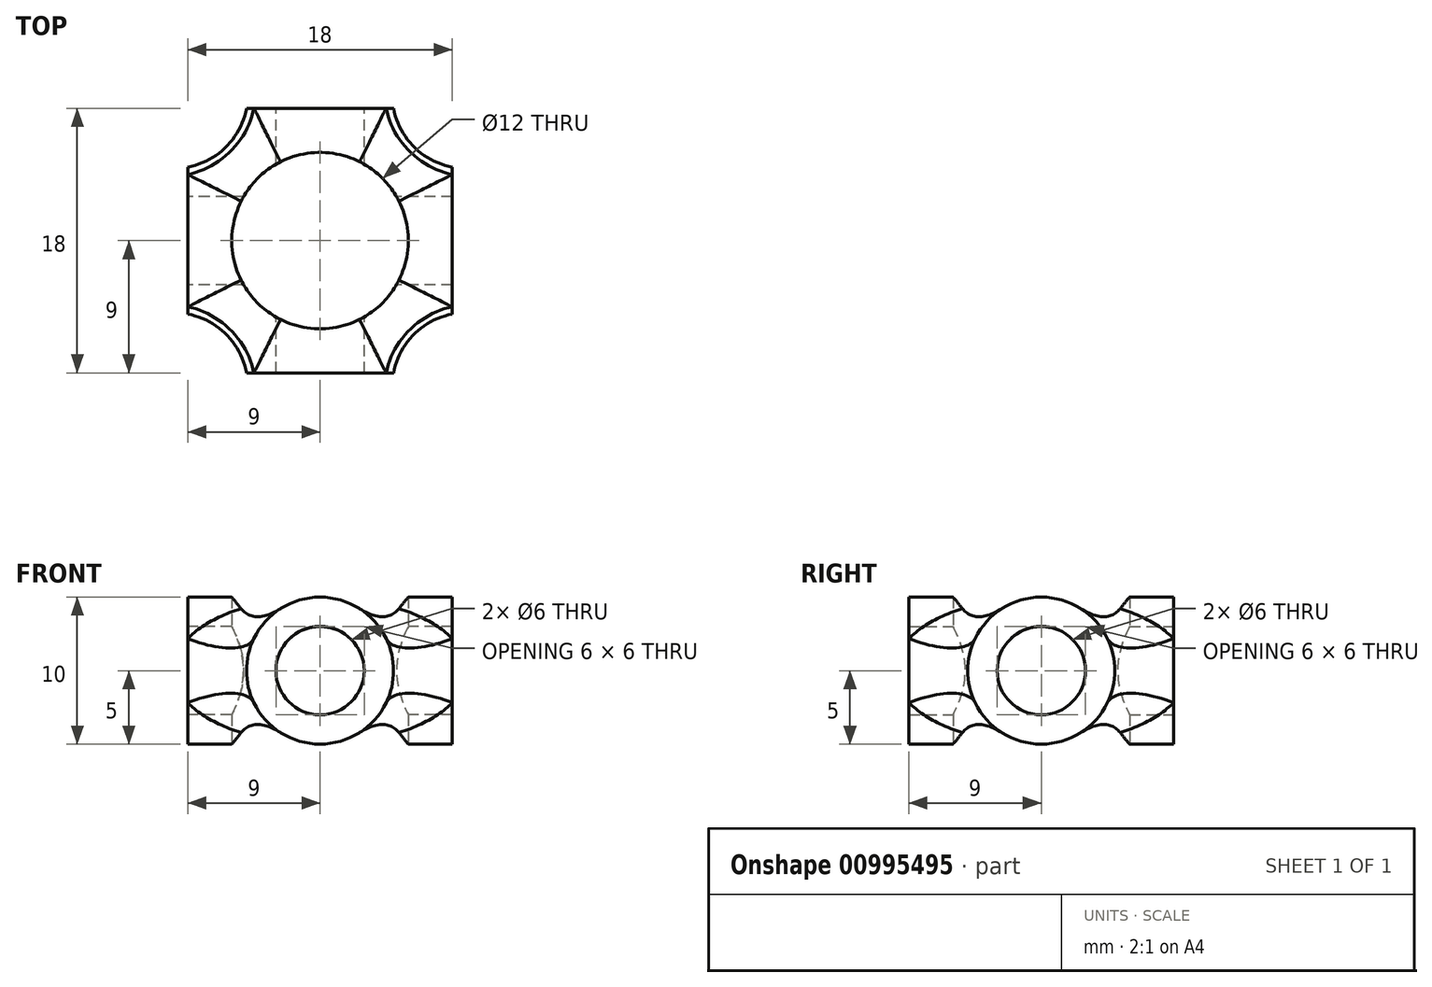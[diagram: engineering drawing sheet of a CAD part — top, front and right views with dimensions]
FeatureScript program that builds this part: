
annotation { "Feature Type Name" : "Feature", "Feature Type Description" : "" }
export const myFeature = defineFeature(function(context is Context, id is Id, definition is map)
    precondition{}
    {
        {
            var Q0;
            Q0=qCreatedBy(makeId("Front.planeOp"),FACE);
            var sketch = newSketch(context, id + "F0", { "sketchPlane" : qUnion([Q0])});
            skCircle(sketch, "E0", {"center": v(0, 0) * mm, "radius": 3 * mm});
            skCircle(sketch, "E1", {"center": v(0, 0) * mm, "radius": 5 * mm});
            skSolve(sketch);
        }
        {
            var Q0;
            Q0 = qSketchRegion(id + "F0", true);
            extrude(context, id + "F1", {"entities" : qUnion([Q0]), "endBound" : BoundingType.SYMMETRIC, "depth" : 18 * mm, "offsetDistance" : 25 * mm});
        }
        {
            var Q0;
            Q0=qCreatedBy(makeId("Right.planeOp"),FACE);
            var sketch = newSketch(context, id + "F2", { "sketchPlane" : qUnion([Q0])});
            skCircle(sketch, "E2", {"center": v(0, 0) * mm, "radius": 5 * mm});
            skCircle(sketch, "E3", {"center": v(0, 0) * mm, "radius": 3 * mm});
            skSolve(sketch);
        }
        {
            var Q0;
            Q0 = qSketchRegion(id + "F2", true);
            extrude(context, id + "F3", {"entities" : qUnion([Q0]), "operationType" : NewBodyOperationType.ADD, "endBound" : BoundingType.SYMMETRIC, "depth" : 18 * mm, "offsetDistance" : 25 * mm});
        }
        {
            var Q0;
            Q0=makeQuery(id+"F3.boolean.opBoolean","INTERSECT",EDGE,{"disambiguationData":[OD(2.0)],"derivedFrom":[makeQuery(id+"F1.opExtrude","SWEPT_FACE",FACE,{"disambiguationData":[OSD([sQuery(id+"F0.wireOp",EDGE,"E1")])]}),makeQuery(id+"F3.opExtrude","SWEPT_FACE",FACE,{"disambiguationData":[OSD([sQuery(id+"F2.wireOp",EDGE,"E2")])]})]});
            var Q1;
            Q1=makeQuery(id+"F3.boolean.opBoolean","INTERSECT",EDGE,{"disambiguationData":[OD(1.0)],"derivedFrom":[makeQuery(id+"F1.opExtrude","SWEPT_FACE",FACE,{"disambiguationData":[OSD([sQuery(id+"F0.wireOp",EDGE,"E1")])]}),makeQuery(id+"F3.opExtrude","SWEPT_FACE",FACE,{"disambiguationData":[OSD([sQuery(id+"F2.wireOp",EDGE,"E2")])]})]});
            var Q2;
            Q2=makeQuery(id+"F3.boolean.opBoolean","INTERSECT",EDGE,{"disambiguationData":[OD(3.0)],"derivedFrom":[makeQuery(id+"F1.opExtrude","SWEPT_FACE",FACE,{"disambiguationData":[OSD([sQuery(id+"F0.wireOp",EDGE,"E1")])]}),makeQuery(id+"F3.opExtrude","SWEPT_FACE",FACE,{"disambiguationData":[OSD([sQuery(id+"F2.wireOp",EDGE,"E2")])]})]});
            var Q3;
            Q3=makeQuery(id+"F3.boolean.opBoolean","INTERSECT",EDGE,{"disambiguationData":[OD(0.0)],"derivedFrom":[makeQuery(id+"F1.opExtrude","SWEPT_FACE",FACE,{"disambiguationData":[OSD([sQuery(id+"F0.wireOp",EDGE,"E1")])]}),makeQuery(id+"F3.opExtrude","SWEPT_FACE",FACE,{"disambiguationData":[OSD([sQuery(id+"F2.wireOp",EDGE,"E2")])]})]});
            fillet(context, id + "F4", {"entities" : qUnion([Q0, Q1, Q2, Q3]), "radius" : 5 * mm, "tangentPropagation" : true, "allowEdgeOverflow" : false});
        }
        {
            var Q0;
            Q0=qCreatedBy(makeId("Top.planeOp"),FACE);
            var sketch = newSketch(context, id + "F5", { "sketchPlane" : qUnion([Q0])});
            skCircle(sketch, "E4", {"center": v(0, 0) * mm, "radius": 6 * mm});
            skSolve(sketch);
        }
        {
            var Q0;
            Q0 = qSketchRegion(id + "F5", true);
            extrude(context, id + "F6", {"entities" : qUnion([Q0]), "operationType" : NewBodyOperationType.REMOVE, "endBound" : BoundingType.THROUGH_ALL, "depth" : 25 * mm, "offsetDistance" : 25 * mm, "hasSecondDirection" : true, "secondDirectionBound" : SecondDirectionBoundingType.THROUGH_ALL, "secondDirectionOppositeDirection" : true, "secondDirectionDepth" : 25 * mm});
        }
    });
